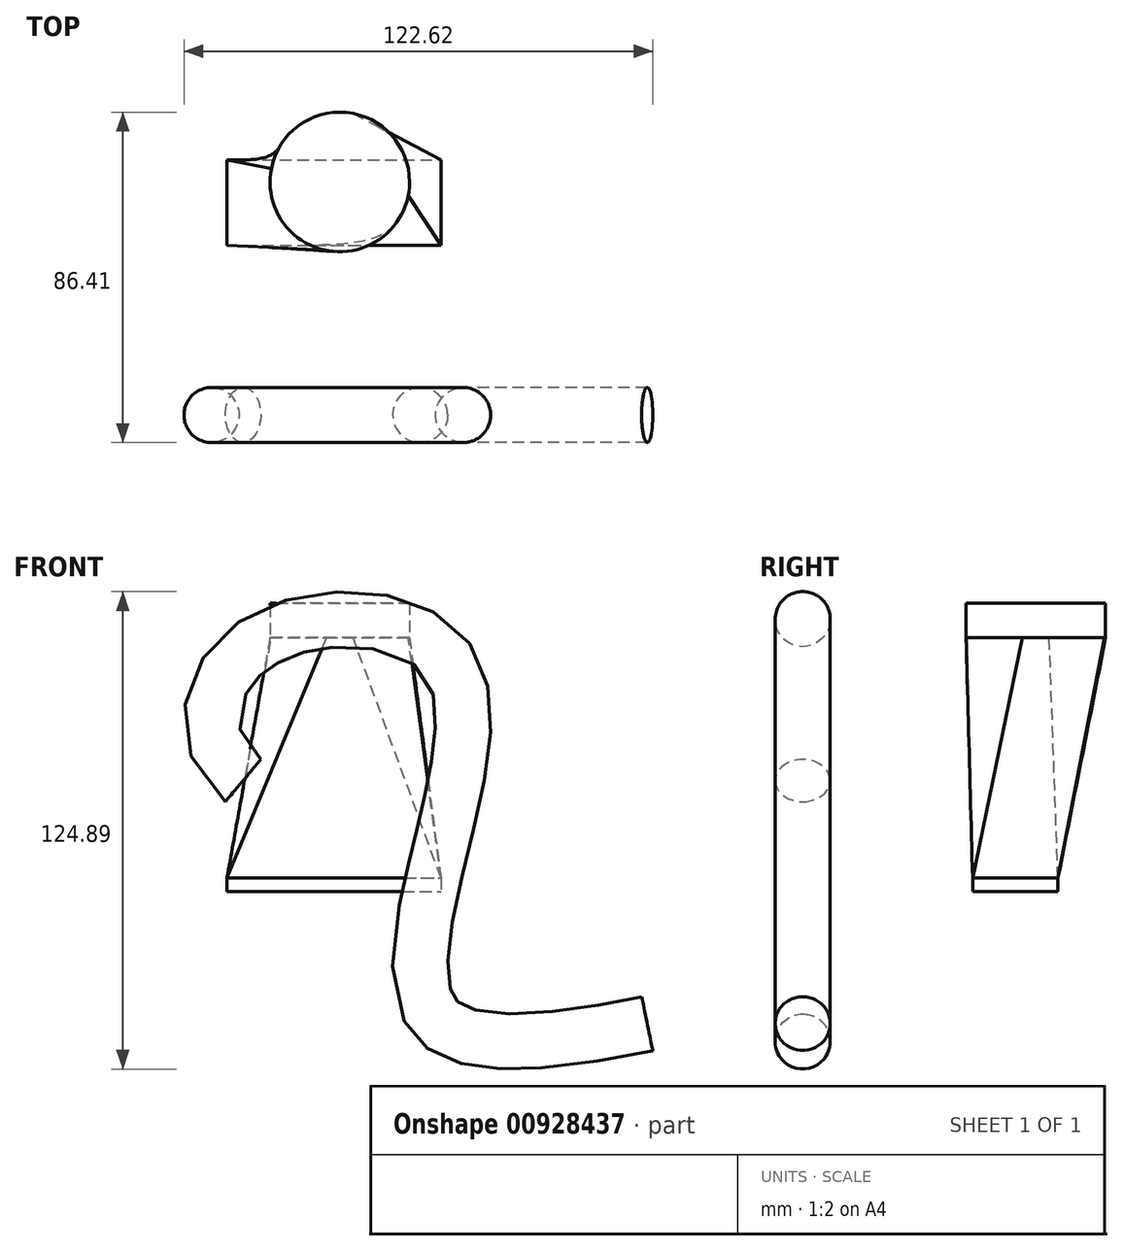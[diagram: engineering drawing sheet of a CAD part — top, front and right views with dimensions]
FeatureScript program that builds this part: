
annotation { "Feature Type Name" : "Feature", "Feature Type Description" : "" }
export const myFeature = defineFeature(function(context is Context, id is Id, definition is map)
    precondition{}
    {
        {
            var Q0;
            Q0=qCreatedBy(makeId("Front.planeOp"),FACE);
            var sketch = newSketch(context, id + "F0", { "sketchPlane" : qUnion([Q0])});
            skFitSpline(sketch, "E0", {"points": [v(53.94, -34.52) * mm, v(0, -34.52) * mm, v(0, 11.55) * mm, v(0, 62.86) * mm, v(-48.66, 64.65) * mm, v(-51.78, 28.97) * mm], "startDerivative": vector(-245.35, -50.77) * mm, "endDerivative": vector(232.52, -194.1) * mm});
            skSolve(sketch);
        }
        {
            var Q0;
            Q0=sQuery(id+"F0.wireOp",VERTEX,"E0.start");
            var Q1;
            Q1=sQuery(id+"F0.wireOp",EDGE,"E0");
            cPlane(context, id + "F1", {"entities" : qUnion([Q0, Q1]), "cplaneType" : CPlaneType.CURVE_POINT, "offset" : 25 * mm, "width" : 150 * mm, "height" : 150 * mm});
        }
        {
            var Q0;
            Q0=qCreatedBy(id+"F1.planeOp",FACE);
            var sketch = newSketch(context, id + "F2", { "sketchPlane" : qUnion([Q0])});
            skCircle(sketch, "E1", {"center": v(0, -44.78) * mm, "radius": 7.2 * mm});
            skSolve(sketch);
        }
        {
            var Q0;
            Q0=makeQuery(id+"F2.imprint","IMPRINT",FACE,{"disambiguationData":[TD([[makeQuery(id+"F2.imprint","IMPRINT",EDGE,{"derivedFrom":sQuery(id+"F2.wireOp",EDGE,"E1")}),1.0]])]});
            var Q1;
            Q1=sQuery(id+"F0.wireOp",EDGE,"E0");
            sweep(context, id + "F3", {"profiles" : qUnion([Q0]), "path" : qUnion([Q1])});
        }
        {
            var Q0;
            Q0=qCreatedBy(makeId("Top.planeOp"),FACE);
            var sketch = newSketch(context, id + "F4", { "sketchPlane" : qUnion([Q0])});
            skLineSegment(sketch, "E2.bottom", {"start": v(-55.94, 66.75) * mm, "end": v(0, 66.75) * mm});
            skLineSegment(sketch, "E2.top", {"start": v(-55.94, 44.42) * mm, "end": v(0, 44.42) * mm});
            skLineSegment(sketch, "E2.left", {"start": v(-55.94, 66.75) * mm, "end": v(-55.94, 44.42) * mm});
            skLineSegment(sketch, "E2.right", {"start": v(0, 66.75) * mm, "end": v(0, 44.42) * mm});
            skSolve(sketch);
        }
        {
            var Q0;
            Q0 = qSketchRegion(id + "F4", true);
            extrude(context, id + "F5", {"entities" : qUnion([Q0]), "depth" : 3.5 * mm, "offsetDistance" : 25 * mm});
        }
        {
            var Q0;
            Q0=makeQuery(id+"F5.opExtrude","CAP_FACE",FACE,{"disambiguationData":[OSD([sQuery(id+"F4.wireOp",EDGE,"E2.bottom"),sQuery(id+"F4.wireOp",EDGE,"E2.top"),sQuery(id+"F4.wireOp",EDGE,"E2.left"),sQuery(id+"F4.wireOp",EDGE,"E2.right")])],"isStart":false});
            cPlane(context, id + "F6", {"entities" : qUnion([Q0]), "cplaneType" : CPlaneType.OFFSET, "offset" : 62.9 * mm, "width" : 150 * mm, "height" : 150 * mm});
        }
        {
            var Q0;
            Q0=qCreatedBy(id+"F6.planeOp",FACE);
            var sketch = newSketch(context, id + "F7", { "sketchPlane" : qUnion([Q0])});
            skCircle(sketch, "E3", {"center": v(-26.45, 60.96) * mm, "radius": 18.25 * mm});
            skSolve(sketch);
        }
        {
            var Q0;
            Q0=makeQuery(id+"F5.opExtrude","CAP_EDGE",EDGE,{"disambiguationData":[OSD([sQuery(id+"F4.wireOp",EDGE,"E2.left")])],"isStart":false});
            cPoint(context, id + "F8", {"entities" : qUnion([Q0]), "parameter" : 0.5});
        }
        {
            var Q0;
            Q0 = qCreatedBy(id + "F8" ,VERTEX);
            var Q1;
            Q1=makeQuery(id+"F5.opExtrude","CAP_EDGE",EDGE,{"disambiguationData":[OSD([sQuery(id+"F4.wireOp",EDGE,"E2.bottom")])],"isStart":false});
            cPlane(context, id + "F9", {"entities" : qUnion([Q0, Q1]), "cplaneType" : CPlaneType.LINE_ANGLE, "offset" : 25 * mm, "angle" : 145 * degree, "oppositeDirection" : true, "width" : 150 * mm, "height" : 150 * mm});
        }
        {
            var Q0;
            Q0=makeQuery(id+"F7.imprint","IMPRINT",FACE,{"disambiguationData":[TD([[makeQuery(id+"F7.imprint","IMPRINT",EDGE,{"derivedFrom":sQuery(id+"F7.wireOp",EDGE,"E3")}),1.0]])]});
            var Q1;
            Q1=sQuery(id+"F7.wireOp",EDGE,"E3");
            extrude(context, id + "F10", {"entities" : qUnion([Q0]), "surfaceEntities" : qUnion([Q1]), "depth" : 9 * mm, "offsetDistance" : 25 * mm});
        }
        {
            var Q0;
            Q0=makeQuery(id+"F5.opExtrude","CAP_FACE",FACE,{"disambiguationData":[OSD([sQuery(id+"F4.wireOp",EDGE,"E2.bottom"),sQuery(id+"F4.wireOp",EDGE,"E2.top"),sQuery(id+"F4.wireOp",EDGE,"E2.left"),sQuery(id+"F4.wireOp",EDGE,"E2.right")])],"isStart":false});
            var Q1;
            Q1=makeQuery(id+"F10.opExtrude","CAP_FACE",FACE,{"disambiguationData":[OSD([sQuery(id+"F7.wireOp",EDGE,"E3")])],"isStart":true});
            loft(context, id + "F11", {"operationType" : NewBodyOperationType.ADD, "sheetProfilesArray" : [{ "sheetProfileEntities" : qUnion([Q0]) }, { "sheetProfileEntities" : qUnion([Q1]) }]});
        }
    });
